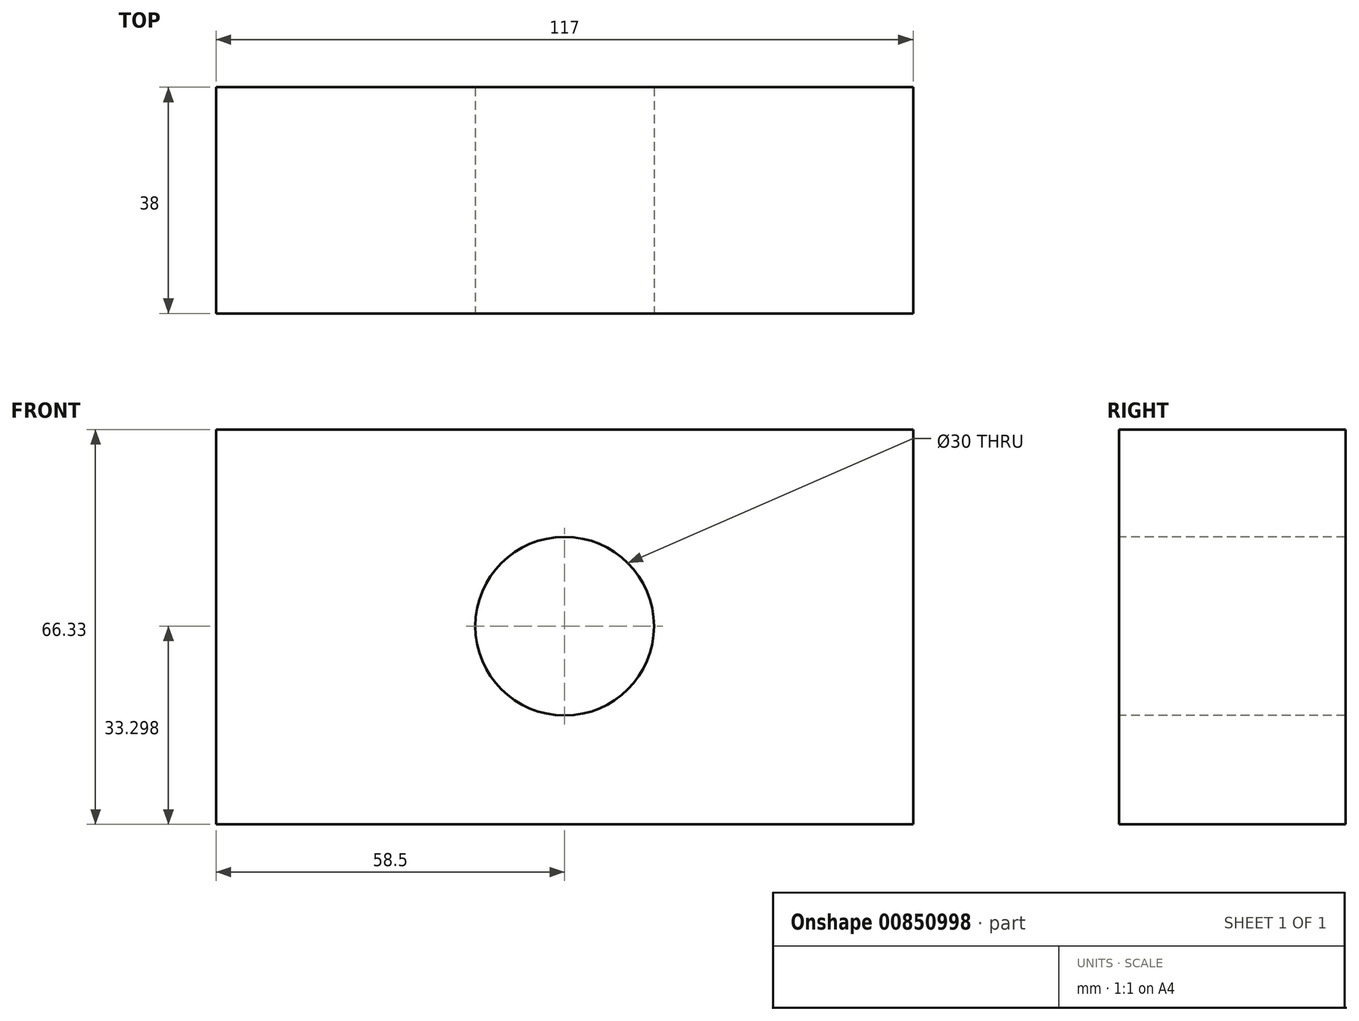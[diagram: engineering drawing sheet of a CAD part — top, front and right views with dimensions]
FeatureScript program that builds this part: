
annotation { "Feature Type Name" : "Feature", "Feature Type Description" : "" }
export const myFeature = defineFeature(function(context is Context, id is Id, definition is map)
    precondition{}
    {
        {
            var Q0;
            Q0=qCreatedBy(makeId("Front.planeOp"),FACE);
            var sketch = newSketch(context, id + "F0", { "sketchPlane" : qUnion([Q0])});
            skLineSegment(sketch, "E0.bottom", {"start": v(-58.5, 32.98) * mm, "end": v(58.5, 32.98) * mm});
            skLineSegment(sketch, "E0.top", {"start": v(-58.5, -33.35) * mm, "end": v(58.5, -33.35) * mm});
            skLineSegment(sketch, "E0.left", {"start": v(-58.5, 32.98) * mm, "end": v(-58.5, -33.35) * mm});
            skLineSegment(sketch, "E0.right", {"start": v(58.5, 32.98) * mm, "end": v(58.5, -33.35) * mm});
            skSolve(sketch);
        }
        {
            var Q0;
            Q0 = qSketchRegion(id + "F0", true);
            extrude(context, id + "F1", {"entities" : qUnion([Q0]), "depth" : 38 * mm, "offsetDistance" : 25 * mm});
        }
        {
            var Q0;
            Q0=makeQuery(id+"F1.opExtrude","CAP_FACE",FACE,{"disambiguationData":[OSD([sQuery(id+"F0.wireOp",EDGE,"E0.bottom"),sQuery(id+"F0.wireOp",EDGE,"E0.top"),sQuery(id+"F0.wireOp",EDGE,"E0.left"),sQuery(id+"F0.wireOp",EDGE,"E0.right")])],"isStart":false});
            var sketch = newSketch(context, id + "F2", { "sketchPlane" : qUnion([Q0])});
            skSolve(sketch);
        }
        {
            var Q0;
            Q0=makeQuery(id+"F2.imprint","IMPRINT",FACE,{"disambiguationData":[TD([[makeQuery(id+"F2.imprint","IMPRINT",EDGE,{"derivedFrom":makeQuery(id+"F1.opExtrude","CAP_EDGE",EDGE,{"disambiguationData":[OSD([sQuery(id+"F0.wireOp",EDGE,"E0.bottom")])],"isStart":false})}),-1.0]])]});
            var sketch = newSketch(context, id + "F3", { "sketchPlane" : qUnion([Q0])});
            skCircle(sketch, "E1", {"center": v(0, -0.05) * mm, "radius": 15 * mm});
            skSolve(sketch);
        }
        {
            var Q0;
            Q0 = qSketchRegion(id + "F3", true);
            extrude(context, id + "F4", {"entities" : qUnion([Q0]), "operationType" : NewBodyOperationType.REMOVE, "endBound" : BoundingType.THROUGH_ALL, "oppositeDirection" : true, "depth" : 25 * mm, "offsetDistance" : 25 * mm});
        }
    });
